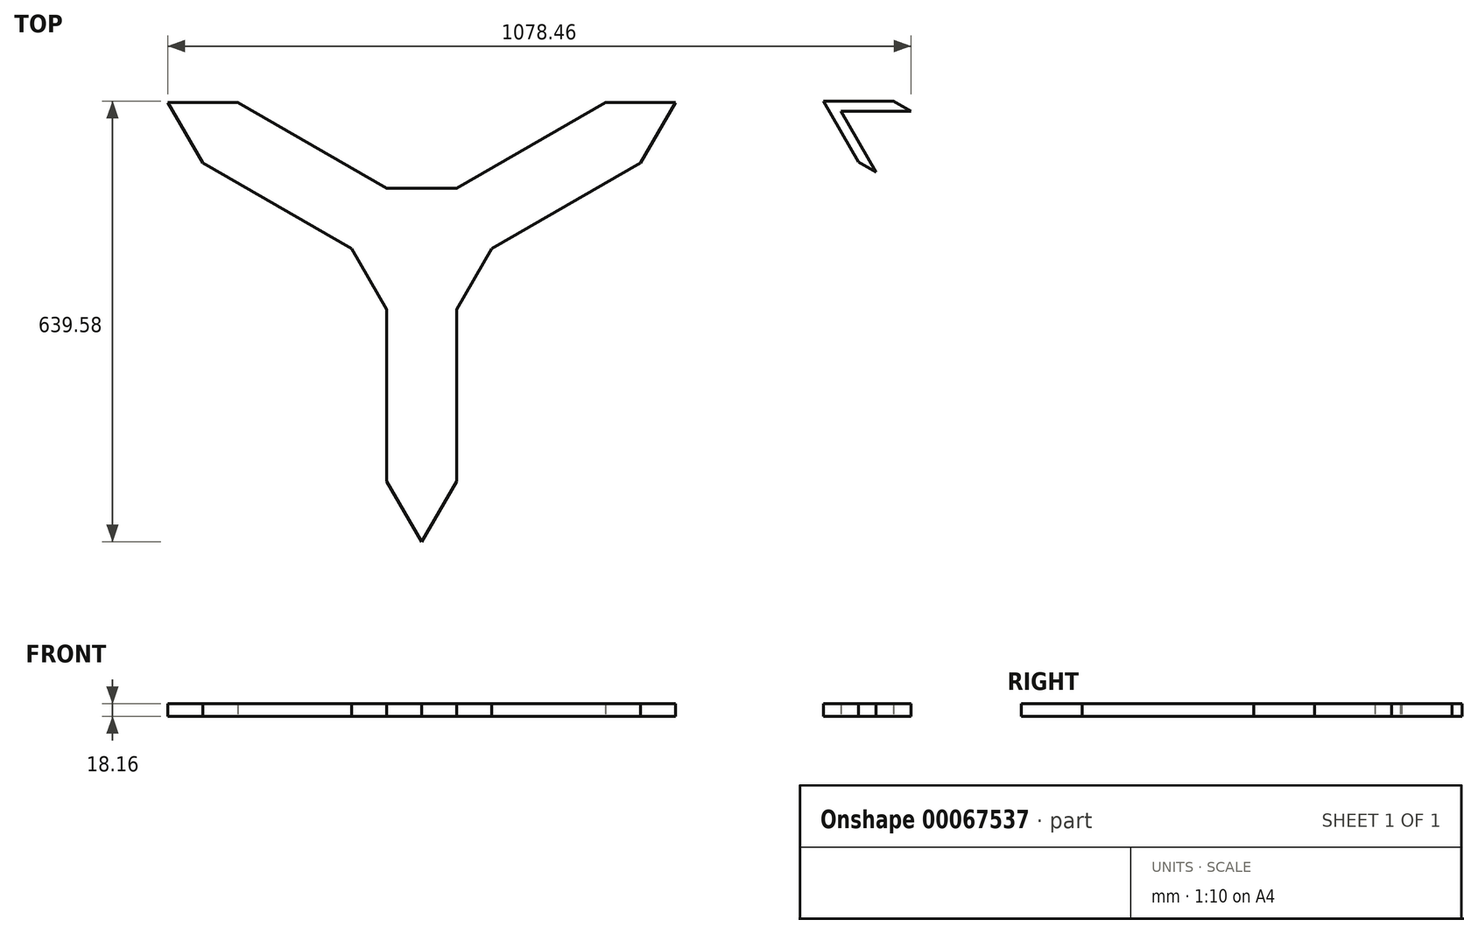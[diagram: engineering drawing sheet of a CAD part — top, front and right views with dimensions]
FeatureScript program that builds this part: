
annotation { "Feature Type Name" : "Feature", "Feature Type Description" : "" }
export const myFeature = defineFeature(function(context is Context, id is Id, definition is map)
    precondition{}
    {
        {
            var Q0;
            Q0=qCreatedBy(makeId("Top.planeOp"),FACE);
            var sketch = newSketch(context, id + "F0", { "sketchPlane" : qUnion([Q0])});
            skCircle(sketch, "E0.cCircle", {"center": v(0, 0) * mm, "radius": 212.64 * mm, "construction": true});
            skLineSegment(sketch, "E0.0", {"start": v(-368.3, 212.64) * mm, "end": v(368.3, 212.64) * mm, "construction": true});
            skLineSegment(sketch, "E0.1", {"start": v(368.3, 212.64) * mm, "end": v(0, -425.28) * mm, "construction": true});
            skLineSegment(sketch, "E0.2", {"start": v(0, -425.28) * mm, "end": v(-368.3, 212.64) * mm, "construction": true});
            skPoint(sketch, "E0.0.midPoint", {"position": v(0, 212.64) * mm});
            skCircle(sketch, "E1.cCircle", {"center": v(0, 0) * mm, "radius": 87.99 * mm, "construction": true});
            skLineSegment(sketch, "E1.0", {"start": v(-50.8, 87.99) * mm, "end": v(50.8, 87.99) * mm});
            skLineSegment(sketch, "E1.1", {"start": v(50.8, 87.99) * mm, "end": v(101.6, 0) * mm});
            skLineSegment(sketch, "E1.2", {"start": v(101.6, 0) * mm, "end": v(50.8, -87.99) * mm});
            skLineSegment(sketch, "E1.3", {"start": v(50.8, -87.99) * mm, "end": v(-50.8, -87.99) * mm});
            skLineSegment(sketch, "E1.4", {"start": v(-50.8, -87.99) * mm, "end": v(-101.6, 0) * mm});
            skLineSegment(sketch, "E1.5", {"start": v(-101.6, 0) * mm, "end": v(-50.8, 87.99) * mm});
            skPoint(sketch, "E1.0.midPoint", {"position": v(0, 87.99) * mm});
            skLineSegment(sketch, "E2", {"start": v(-101.6, 0) * mm, "end": v(-317.5, 124.65) * mm});
            skLineSegment(sketch, "E3", {"start": v(-50.8, 87.99) * mm, "end": v(-266.7, 212.64) * mm});
            skLineSegment(sketch, "E4.1.0", {"start": v(-50.8, -87.99) * mm, "end": v(-50.8, -337.29) * mm});
            skLineSegment(sketch, "E4.1.1", {"start": v(50.8, -87.99) * mm, "end": v(50.8, -337.29) * mm});
            skLineSegment(sketch, "E4.2.0", {"start": v(101.6, 0) * mm, "end": v(317.5, 124.65) * mm});
            skLineSegment(sketch, "E4.2.1", {"start": v(50.8, 87.99) * mm, "end": v(266.7, 212.64) * mm});
            skPoint(sketch, "E5.orphan", {"position": v(266.7, 212.64) * mm});
            skPoint(sketch, "E6.orphan", {"position": v(317.5, 124.65) * mm});
            skPoint(sketch, "E7.orphan", {"position": v(-266.7, 212.64) * mm});
            skPoint(sketch, "E8.orphan", {"position": v(-317.5, 124.65) * mm});
            skPoint(sketch, "E9.orphan", {"position": v(-50.8, -337.29) * mm});
            skPoint(sketch, "E10.orphan", {"position": v(50.8, -337.29) * mm});
            skLineSegment(sketch, "E11", {"start": v(-317.5, 124.65) * mm, "end": v(-368.3, 212.64) * mm});
            skLineSegment(sketch, "E12", {"start": v(-266.7, 212.64) * mm, "end": v(-368.3, 212.64) * mm});
            skLineSegment(sketch, "E13", {"start": v(266.7, 212.64) * mm, "end": v(368.3, 212.64) * mm});
            skLineSegment(sketch, "E14", {"start": v(368.3, 212.64) * mm, "end": v(317.5, 124.65) * mm});
            skLineSegment(sketch, "E15", {"start": v(-50.8, -337.29) * mm, "end": v(0, -425.28) * mm});
            skLineSegment(sketch, "E16", {"start": v(0, -425.28) * mm, "end": v(50.8, -337.29) * mm});
            skLineSegment(sketch, "E17", {"start": v(633.96, 126.3) * mm, "end": v(583.16, 214.3) * mm});
            skLineSegment(sketch, "E18.trimOffspring", {"start": v(659.36, 111.64) * mm, "end": v(608.56, 199.63) * mm});
            skLineSegment(sketch, "E19.0", {"start": v(608.56, 199.63) * mm, "end": v(710.16, 199.63) * mm});
            skPoint(sketch, "E20.orphan", {"position": v(633.96, 126.3) * mm});
            skLineSegment(sketch, "E21", {"start": v(684.76, 214.3) * mm, "end": v(583.16, 214.3) * mm});
            skPoint(sketch, "E22.orphan", {"position": v(684.76, 214.3) * mm});
            skLineSegment(sketch, "E23", {"start": v(684.76, 214.3) * mm, "end": v(710.16, 199.63) * mm});
            skLineSegment(sketch, "E24", {"start": v(633.96, 126.3) * mm, "end": v(659.36, 111.64) * mm});
            skSolve(sketch);
        }
        {
            var Q0;
            Q0=makeQuery(id+"F0.imprint","IMPRINT",FACE,{"disambiguationData":[TD([[makeQuery(id+"F0.imprint","IMPRINT",EDGE,{"derivedFrom":sQuery(id+"F0.wireOp",EDGE,"E1.5")}),1.0]])]});
            var Q1;
            Q1=makeQuery(id+"F0.imprint","IMPRINT",FACE,{"disambiguationData":[TD([[makeQuery(id+"F0.imprint","IMPRINT",EDGE,{"derivedFrom":sQuery(id+"F0.wireOp",EDGE,"E1.0")}),-1.0]])]});
            var Q2;
            Q2=makeQuery(id+"F0.imprint","IMPRINT",FACE,{"disambiguationData":[TD([[makeQuery(id+"F0.imprint","IMPRINT",EDGE,{"derivedFrom":sQuery(id+"F0.wireOp",EDGE,"E1.1")}),1.0]])]});
            var Q3;
            Q3=makeQuery(id+"F0.imprint","IMPRINT",FACE,{"disambiguationData":[TD([[makeQuery(id+"F0.imprint","IMPRINT",EDGE,{"derivedFrom":sQuery(id+"F0.wireOp",EDGE,"E1.3")}),1.0]])]});
            var Q4;
            Q4=makeQuery(id+"F0.imprint","IMPRINT",FACE,{"disambiguationData":[TD([[makeQuery(id+"F0.imprint","IMPRINT",EDGE,{"derivedFrom":sQuery(id+"F0.wireOp",EDGE,"E17")}),-1.0]])]});
            extrude(context, id + "F1", {"entities" : qUnion([Q0, Q1, Q2, Q3, Q4]), "depth" : 18.16 * mm});
        }
    });
